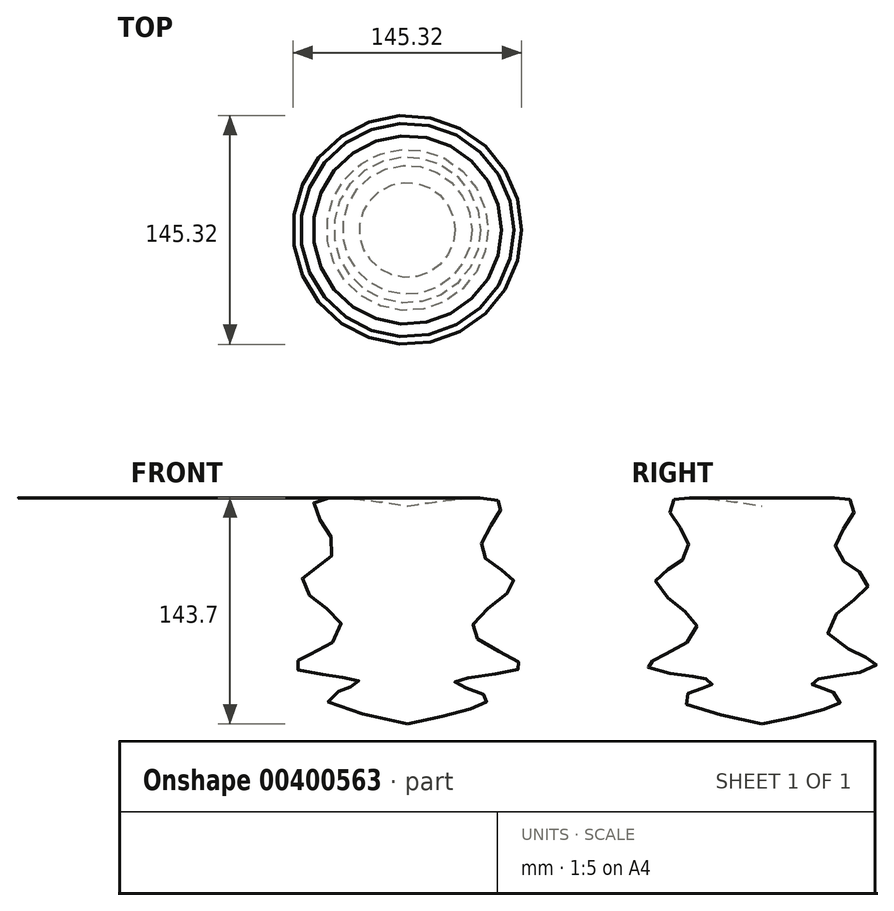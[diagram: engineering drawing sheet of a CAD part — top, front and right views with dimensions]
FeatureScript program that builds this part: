
annotation { "Feature Type Name" : "Feature", "Feature Type Description" : "" }
export const myFeature = defineFeature(function(context is Context, id is Id, definition is map)
    precondition{}
    {
        {
            var Q0;
            Q0=qCreatedBy(makeId("Front.planeOp"),FACE);
            var sketch = newSketch(context, id + "F0", { "sketchPlane" : qUnion([Q0])});
            skLineSegment(sketch, "E0", {"start": v(-46.77, 65.63) * mm, "end": v(-46.77, -72.97) * mm});
            skFitSpline(sketch, "E1", {"points": [v(-46.77, 65.63) * mm, v(13.1, 65.63) * mm, v(0, 36.69) * mm, v(20.95, 16.34) * mm, v(-5.61, -13.78) * mm, v(25.82, -36.5) * mm, v(-16.46, -46.1) * mm, v(3.74, -55.6) * mm, v(-46.77, -72.97) * mm], "startDerivative": vector(578.67, 85.59) * mm, "endDerivative": vector(-576.09, -120.73) * mm});
            skSolve(sketch);
        }
        {
            var Q0;
            Q0=makeQuery(id+"F0.imprint","IMPRINT",FACE,{"disambiguationData":[TD([[makeQuery(id+"F0.imprint","IMPRINT",EDGE,{"derivedFrom":sQuery(id+"F0.wireOp",EDGE,"E0")}),1.0]])]});
            var Q1;
            Q1=sQuery(id+"F0.wireOp",EDGE,"E0");
            revolve(context, id + "F1", {"entities" : qUnion([Q0]), "axis" : qUnion([Q1]), "revolveType" : RevolveType.FULL});
        }
    });
